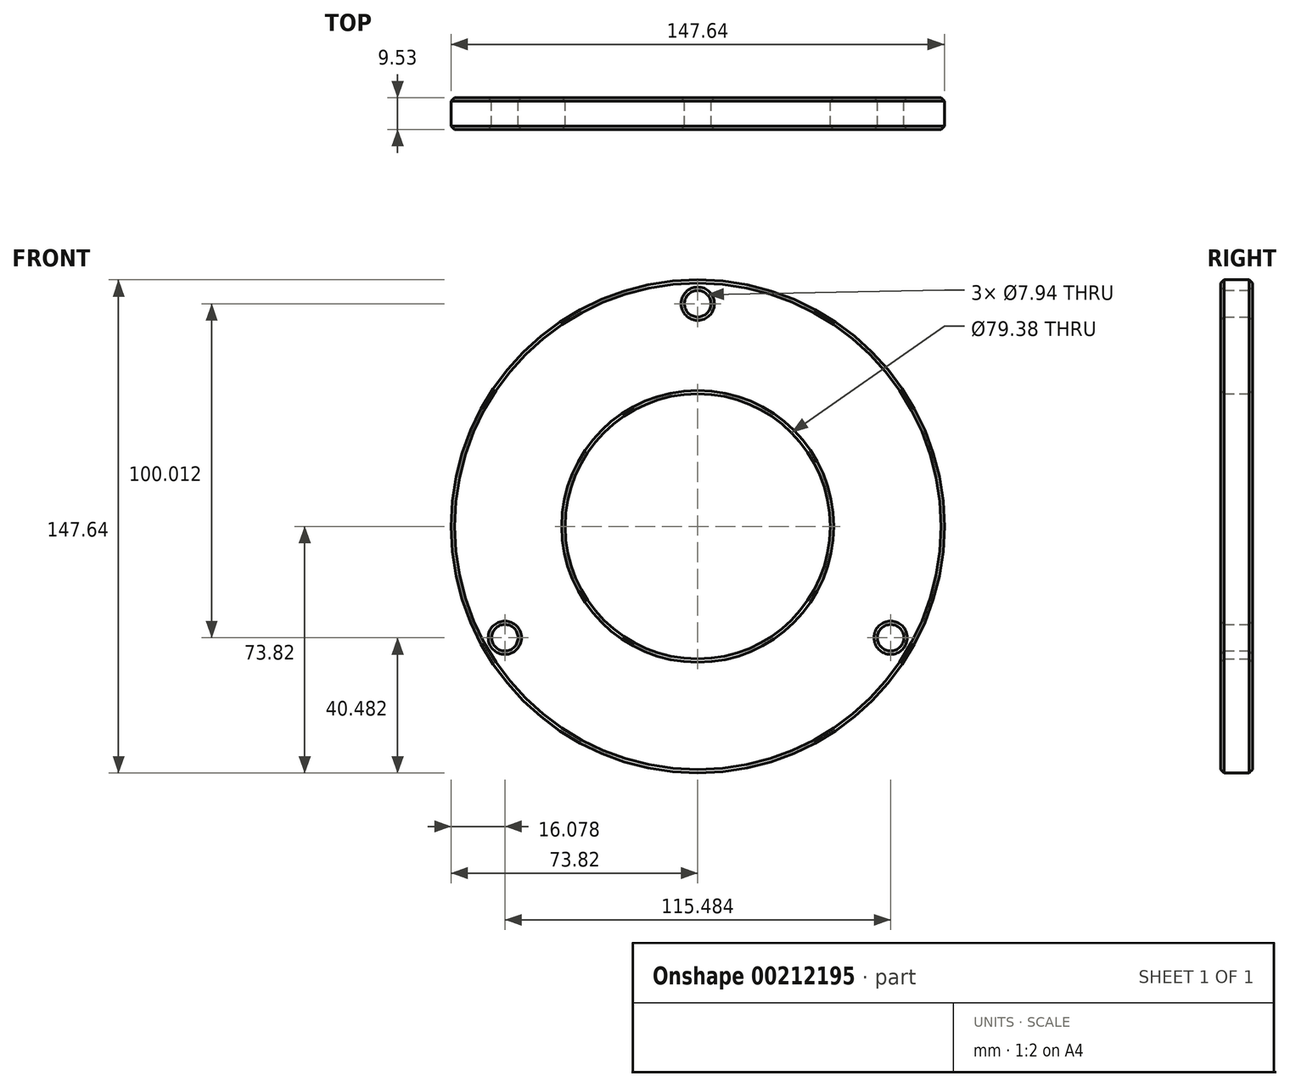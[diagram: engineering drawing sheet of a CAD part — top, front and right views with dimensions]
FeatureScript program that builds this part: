
annotation { "Feature Type Name" : "Feature", "Feature Type Description" : "" }
export const myFeature = defineFeature(function(context is Context, id is Id, definition is map)
    precondition{}
    {
        {
            var Q0;
            Q0=qCreatedBy(makeId("Front.planeOp"),FACE);
            var sketch = newSketch(context, id + "F0", { "sketchPlane" : qUnion([Q0])});
            skCircle(sketch, "E0", {"center": v(0, 0) * mm, "radius": 73.82 * mm});
            skCircle(sketch, "E1", {"center": v(0, 0) * mm, "radius": 66.68 * mm, "construction": true});
            skCircle(sketch, "E2", {"center": v(0, 0) * mm, "radius": 39.69 * mm});
            skCircle(sketch, "E3", {"center": v(0, 66.68) * mm, "radius": 3.97 * mm});
            skCircle(sketch, "E4.1.0", {"center": v(-57.74, -33.34) * mm, "radius": 3.97 * mm});
            skCircle(sketch, "E4.2.0", {"center": v(57.74, -33.34) * mm, "radius": 3.97 * mm});
            skSolve(sketch);
        }
        {
            var Q0;
            Q0=makeQuery(id+"F0.imprint","IMPRINT",FACE,{"disambiguationData":[TD([[makeQuery(id+"F0.imprint","IMPRINT",EDGE,{"derivedFrom":sQuery(id+"F0.wireOp",EDGE,"E0")}),1.0]])]});
            extrude(context, id + "F1", {"entities" : qUnion([Q0]), "depth" : 9.52 * mm});
        }
        {
            var Q0;
            Q0=makeQuery(id+"F1.opExtrude","CAP_FACE",FACE,{"disambiguationData":[OSD([sQuery(id+"F0.wireOp",EDGE,"E0"),sQuery(id+"F0.wireOp",EDGE,"E2"),sQuery(id+"F0.wireOp",EDGE,"E3"),sQuery(id+"F0.wireOp",EDGE,"E4.1.0"),sQuery(id+"F0.wireOp",EDGE,"E4.2.0")])],"isStart":false});
            var Q1;
            Q1=makeQuery(id+"F1.opExtrude","CAP_FACE",FACE,{"disambiguationData":[OSD([sQuery(id+"F0.wireOp",EDGE,"E0"),sQuery(id+"F0.wireOp",EDGE,"E2"),sQuery(id+"F0.wireOp",EDGE,"E3"),sQuery(id+"F0.wireOp",EDGE,"E4.1.0"),sQuery(id+"F0.wireOp",EDGE,"E4.2.0")])],"isStart":true});
            chamfer(context, id + "F2", {"entities" : qUnion([Q0, Q1]), "width" : 1.02 * mm, "tangentPropagation" : true});
        }
    });
